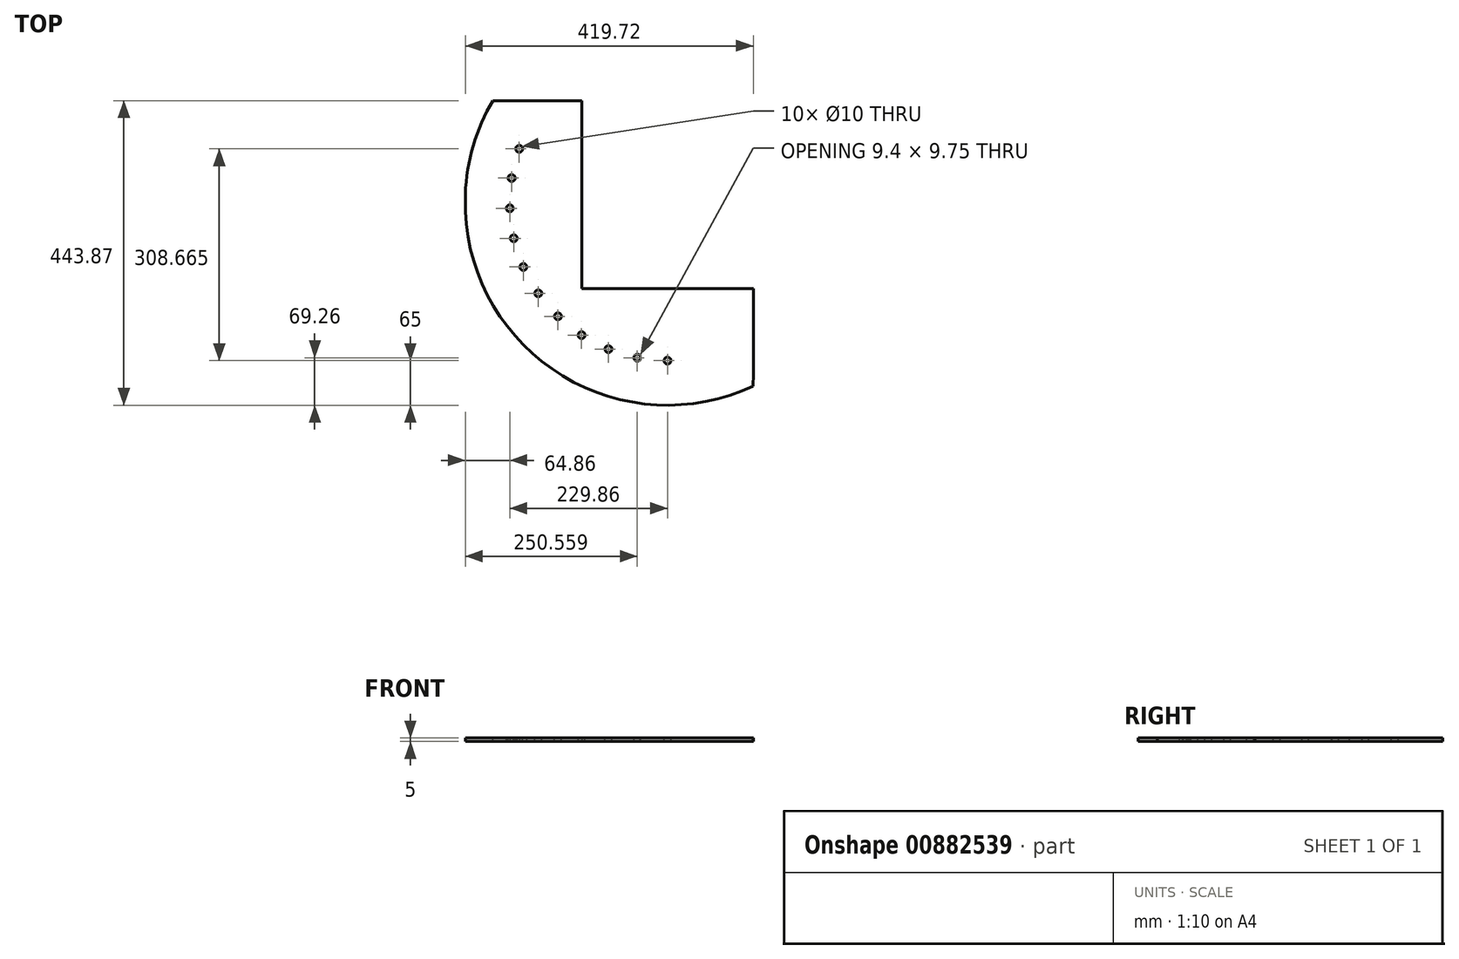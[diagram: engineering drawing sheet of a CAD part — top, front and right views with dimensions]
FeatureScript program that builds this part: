
annotation { "Feature Type Name" : "Feature", "Feature Type Description" : "" }
export const myFeature = defineFeature(function(context is Context, id is Id, definition is map)
    precondition{}
    {
        {
            var Q0;
            Q0=qCreatedBy(makeId("Top.planeOp"),FACE);
            var sketch = newSketch(context, id + "F0", { "sketchPlane" : qUnion([Q0])});
            skLineSegment(sketch, "E0.bottom", {"start": v(125, -125) * mm, "end": v(-125, -125) * mm});
            skLineSegment(sketch, "E0.top", {"start": v(125, 125) * mm, "end": v(-125, 125) * mm});
            skLineSegment(sketch, "E0.left", {"start": v(125, -125) * mm, "end": v(125, 125) * mm});
            skLineSegment(sketch, "E0.right", {"start": v(-125, -125) * mm, "end": v(-125, 125) * mm});
            skPoint(sketch, "E0.middle", {"position": v(0, 0) * mm});
            skLineSegment(sketch, "E1", {"start": v(0, 0) * mm, "end": v(-125, 0) * mm, "construction": true});
            skLineSegment(sketch, "E2.bottom", {"start": v(-349.96, 0) * mm, "end": v(0, 0) * mm});
            skLineSegment(sketch, "E2.left", {"start": v(-349.96, 0) * mm, "end": v(-349.96, 125) * mm});
            skLineSegment(sketch, "E2.right", {"start": v(125, 0) * mm, "end": v(125, 125) * mm});
            skLineSegment(sketch, "E3.MirrorCS", {"start": v(-349.96, 0) * mm, "end": v(-349.96, -249.62) * mm});
            skLineSegment(sketch, "E4.MirrorCS", {"start": v(-349.96, -249.62) * mm, "end": v(125, -249.62) * mm});
            skLineSegment(sketch, "E5.MirrorCS", {"start": v(125, 0) * mm, "end": v(125, -249.62) * mm});
            skLineSegment(sketch, "E6", {"start": v(-349.96, 125) * mm, "end": v(125, 125) * mm});
            skPoint(sketch, "E2.top.start.orphan", {"position": v(-349.96, 249.62) * mm});
            skPoint(sketch, "E7.orphan", {"position": v(125, 249.62) * mm});
            skLineSegment(sketch, "E8", {"start": v(-349.96, 29.15) * mm, "end": v(-125, 29.15) * mm});
            skLineSegment(sketch, "E9", {"start": v(-349.96, -249.62) * mm, "end": v(-349.96, -298.58) * mm});
            skLineSegment(sketch, "E10", {"start": v(-349.96, -298.58) * mm, "end": v(124.79, -298.58) * mm});
            skLineSegment(sketch, "E11", {"start": v(124.79, -298.58) * mm, "end": v(125, -249.62) * mm});
            skLineSegment(sketch, "E12", {"start": v(-294.72, 29.15) * mm, "end": v(-294.72, -298.58) * mm});
            skLineSegment(sketch, "E13", {"start": v(-294.72, 29.15) * mm, "end": v(-294.72, 125) * mm});
            skLineSegment(sketch, "E14", {"start": v(-294.72, 125) * mm, "end": v(-294.72, 148.87) * mm});
            skLineSegment(sketch, "E15", {"start": v(-294.72, 148.87) * mm, "end": v(-125.13, 148.87) * mm});
            skLineSegment(sketch, "E16", {"start": v(-125.13, 148.87) * mm, "end": v(-125, 125) * mm});
            skSolve(sketch);
        }
        {
            var Q0;
            {var subQ0=sQuery(id+"F0.wireOp",EDGE,"E8");var subQ1=sQuery(id+"F0.wireOp",EDGE,"E0.right");var subQ2=makeQuery(id+"F0.imprint","INTERSECT",VERTEX,{"derivedFrom":[subQ1,subQ0]});Q0=makeQuery(id+"F0.imprint","IMPRINT",FACE,{"disambiguationData":[TD([[makeQuery(id+"F0.imprint","IMPRINT",EDGE,{"disambiguationData":[TD([[subQ2,1.0]])],"derivedFrom":subQ1}),1.0]])]});}
            var Q1;
            {var subQ5=sQuery(id+"F0.wireOp",EDGE,"E0.bottom");Q1=makeQuery(id+"F0.imprint","IMPRINT",FACE,{"disambiguationData":[TD([[makeQuery(id+"F0.imprint","IMPRINT",EDGE,{"derivedFrom":subQ5}),1.0]])]});}
            var Q2;
            {var subQ0=sQuery(id+"F0.wireOp",EDGE,"E11");Q2=makeQuery(id+"F0.imprint","IMPRINT",FACE,{"disambiguationData":[TD([[makeQuery(id+"F0.imprint","IMPRINT",EDGE,{"derivedFrom":subQ0}),1.0]])]});}
            var Q3;
            {var subQ4=sQuery(id+"F0.wireOp",EDGE,"E6");var subQ5=sQuery(id+"F0.wireOp",EDGE,"E0.right");var subQ6=makeQuery(id+"F0.imprint","INTERSECT",VERTEX,{"derivedFrom":[subQ5,subQ4]});Q3=makeQuery(id+"F0.imprint","IMPRINT",FACE,{"disambiguationData":[TD([[makeQuery(id+"F0.imprint","IMPRINT",EDGE,{"disambiguationData":[TD([[subQ6,1.0]])],"derivedFrom":subQ5}),1.0]])]});}
            var Q4;
            {var subQ2=sQuery(id+"F0.wireOp",EDGE,"E14");Q4=makeQuery(id+"F0.imprint","IMPRINT",FACE,{"disambiguationData":[TD([[makeQuery(id+"F0.imprint","IMPRINT",EDGE,{"derivedFrom":subQ2}),-1.0]])]});}
            extrude(context, id + "F1", {"entities" : qUnion([Q0, Q1, Q2, Q3, Q4]), "depth" : 5 * mm, "offsetDistance" : 25 * mm});
        }
        {
            var Q0;
            Q0=makeQuery(id+"F1.opExtrude","CAP_FACE",FACE,{"disambiguationData":[OSD([sQuery(id+"F0.wireOp",EDGE,"E0.bottom"),sQuery(id+"F0.wireOp",EDGE,"E0.top"),sQuery(id+"F0.wireOp",EDGE,"E0.left"),sQuery(id+"F0.wireOp",EDGE,"E0.right"),sQuery(id+"F0.wireOp",EDGE,"E2.top"),sQuery(id+"F0.wireOp",EDGE,"E2.left"),sQuery(id+"F0.wireOp",EDGE,"E2.right"),sQuery(id+"F0.wireOp",EDGE,"E3.MirrorCS"),sQuery(id+"F0.wireOp",EDGE,"E4.MirrorCS"),sQuery(id+"F0.wireOp",EDGE,"E5.MirrorCS")])],"isStart":false});
            var sketch = newSketch(context, id + "F2", { "sketchPlane" : qUnion([Q0])});
            skCircle(sketch, "E17", {"center": v(0, 0) * mm, "radius": 270 * mm});
            skCircle(sketch, "E18", {"center": v(0, 0) * mm, "radius": 190 * mm});
            skLineSegment(sketch, "E19", {"start": v(0, 0) * mm, "end": v(-270, 0) * mm, "construction": true});
            skCircle(sketch, "E20", {"center": v(0, 0) * mm, "radius": 230 * mm, "construction": true});
            skCircle(sketch, "E21", {"center": v(-216.13, 78.66) * mm, "radius": 40 * mm});
            skCircle(sketch, "E22", {"center": v(0, -230) * mm, "radius": 40 * mm});
            skLineSegment(sketch, "E23", {"start": v(-216.13, 78.66) * mm, "end": v(0, 0) * mm, "construction": true});
            skLineSegment(sketch, "E24", {"start": v(0, 0) * mm, "end": v(0, -230) * mm, "construction": true});
            skCircle(sketch, "E25", {"center": v(-216.13, 78.66) * mm, "radius": 5 * mm});
            skCircle(sketch, "E26.1.0", {"center": v(-227.17, 35.98) * mm, "radius": 5 * mm});
            skCircle(sketch, "E26.2.0", {"center": v(-229.86, -8.03) * mm, "radius": 5 * mm});
            skCircle(sketch, "E26.3.0", {"center": v(-224.1, -51.74) * mm, "radius": 5 * mm});
            skCircle(sketch, "E26.4.0", {"center": v(-210.12, -93.55) * mm, "radius": 5 * mm});
            skCircle(sketch, "E26.5.0", {"center": v(-188.4, -131.92) * mm, "radius": 5 * mm});
            skCircle(sketch, "E26.6.0", {"center": v(-159.77, -165.45) * mm, "radius": 5 * mm});
            skCircle(sketch, "E26.7.0", {"center": v(-125.27, -192.9) * mm, "radius": 5 * mm});
            skCircle(sketch, "E26.8.0", {"center": v(-86.16, -213.25) * mm, "radius": 5 * mm});
            skCircle(sketch, "E26.9.0", {"center": v(-43.89, -225.77) * mm, "radius": 5 * mm});
            skCircle(sketch, "E26.10.0", {"center": v(0, -230) * mm, "radius": 5 * mm});
            skLineSegment(sketch, "E26.anchor1", {"start": v(0, 0) * mm, "end": v(-216.13, 78.66) * mm, "construction": true});
            skSolve(sketch);
        }
        {
            var Q0;
            Q0=makeQuery(id+"F2.imprint","IMPRINT",FACE,{"disambiguationData":[TD([[makeQuery(id+"F2.imprint","IMPRINT",EDGE,{"derivedFrom":sQuery(id+"F2.wireOp",EDGE,"E26.10.0")}),1.0]])]});
            var Q1;
            {var subQ0=sQuery(id+"F2.wireOp",EDGE,"E26.9.0");var subQ1=sQuery(id+"F2.wireOp",EDGE,"E22");var subQ2=makeQuery(id+"F2.imprint","INTERSECT",VERTEX,{"disambiguationData":[OD(0.0)],"derivedFrom":[subQ1,subQ0]});Q1=makeQuery(id+"F2.imprint","IMPRINT",FACE,{"disambiguationData":[TD([[makeQuery(id+"F2.imprint","IMPRINT",EDGE,{"disambiguationData":[TD([[subQ2,-1.0]])],"derivedFrom":subQ1}),-1.0]])]});}
            var Q2;
            Q2=makeQuery(id+"F2.imprint","IMPRINT",FACE,{"disambiguationData":[TD([[makeQuery(id+"F2.imprint","IMPRINT",EDGE,{"derivedFrom":sQuery(id+"F2.wireOp",EDGE,"E26.8.0")}),1.0]])]});
            var Q3;
            Q3=makeQuery(id+"F2.imprint","IMPRINT",FACE,{"disambiguationData":[TD([[makeQuery(id+"F2.imprint","IMPRINT",EDGE,{"derivedFrom":sQuery(id+"F2.wireOp",EDGE,"E26.7.0")}),1.0]])]});
            var Q4;
            Q4=makeQuery(id+"F2.imprint","IMPRINT",FACE,{"disambiguationData":[TD([[makeQuery(id+"F2.imprint","IMPRINT",EDGE,{"derivedFrom":sQuery(id+"F2.wireOp",EDGE,"E26.5.0")}),1.0]])]});
            var Q5;
            Q5=makeQuery(id+"F2.imprint","IMPRINT",FACE,{"disambiguationData":[TD([[makeQuery(id+"F2.imprint","IMPRINT",EDGE,{"derivedFrom":sQuery(id+"F2.wireOp",EDGE,"E26.6.0")}),1.0]])]});
            var Q6;
            Q6=makeQuery(id+"F2.imprint","IMPRINT",FACE,{"disambiguationData":[TD([[makeQuery(id+"F2.imprint","IMPRINT",EDGE,{"derivedFrom":sQuery(id+"F2.wireOp",EDGE,"E26.4.0")}),1.0]])]});
            var Q7;
            Q7=makeQuery(id+"F2.imprint","IMPRINT",FACE,{"disambiguationData":[TD([[makeQuery(id+"F2.imprint","IMPRINT",EDGE,{"derivedFrom":sQuery(id+"F2.wireOp",EDGE,"E26.3.0")}),1.0]])]});
            var Q8;
            Q8=makeQuery(id+"F2.imprint","IMPRINT",FACE,{"disambiguationData":[TD([[makeQuery(id+"F2.imprint","IMPRINT",EDGE,{"derivedFrom":sQuery(id+"F2.wireOp",EDGE,"E26.2.0")}),1.0]])]});
            var Q9;
            {var subQ0=sQuery(id+"F2.wireOp",EDGE,"E26.1.0");var subQ1=sQuery(id+"F2.wireOp",EDGE,"E21");var subQ2=makeQuery(id+"F2.imprint","INTERSECT",VERTEX,{"disambiguationData":[OD(0.0)],"derivedFrom":[subQ1,subQ0]});Q9=makeQuery(id+"F2.imprint","IMPRINT",FACE,{"disambiguationData":[TD([[makeQuery(id+"F2.imprint","IMPRINT",EDGE,{"disambiguationData":[TD([[subQ2,-1.0]])],"derivedFrom":subQ1}),-1.0]])]});}
            var Q10;
            Q10=makeQuery(id+"F2.imprint","IMPRINT",FACE,{"disambiguationData":[TD([[makeQuery(id+"F2.imprint","IMPRINT",EDGE,{"derivedFrom":sQuery(id+"F2.wireOp",EDGE,"E25")}),1.0]])]});
            var Q11;
            {var subQ0=sQuery(id+"F2.wireOp",EDGE,"E26.1.0");var subQ1=sQuery(id+"F2.wireOp",EDGE,"E21");var subQ2=makeQuery(id+"F2.imprint","INTERSECT",VERTEX,{"disambiguationData":[OD(0.0)],"derivedFrom":[subQ1,subQ0]});Q11=makeQuery(id+"F2.imprint","IMPRINT",FACE,{"disambiguationData":[TD([[makeQuery(id+"F2.imprint","IMPRINT",EDGE,{"disambiguationData":[TD([[subQ2,-1.0]])],"derivedFrom":subQ1}),1.0]])]});}
            extrude(context, id + "F3", {"entities" : qUnion([Q0, Q1, Q2, Q3, Q4, Q5, Q6, Q7, Q8, Q9, Q10, Q11]), "operationType" : NewBodyOperationType.REMOVE, "oppositeDirection" : true, "depth" : 6 * mm, "offsetDistance" : 25 * mm});
        }
        {
            var Q0;
            Q0=makeQuery(id+"F1.opExtrude","CAP_FACE",FACE,{"disambiguationData":[OSD([sQuery(id+"F0.wireOp",EDGE,"E0.bottom"),sQuery(id+"F0.wireOp",EDGE,"E0.right"),sQuery(id+"F0.wireOp",EDGE,"E5.MirrorCS"),sQuery(id+"F0.wireOp",EDGE,"E8"),sQuery(id+"F0.wireOp",EDGE,"E10"),sQuery(id+"F0.wireOp",EDGE,"E11"),sQuery(id+"F0.wireOp",EDGE,"E12")])],"isStart":false});
            var sketch = newSketch(context, id + "F4", { "sketchPlane" : qUnion([Q0])});
            skCircle(sketch, "E27", {"center": v(0, 0) * mm, "radius": 295 * mm});
            skLineSegment(sketch, "E28", {"start": v(178.33, -235) * mm, "end": v(178.33, -361.67) * mm});
            skLineSegment(sketch, "E29", {"start": v(178.33, -361.67) * mm, "end": v(-429.48, -361.67) * mm});
            skLineSegment(sketch, "E30", {"start": v(-429.48, -361.67) * mm, "end": v(-429.48, 76.22) * mm});
            skLineSegment(sketch, "E31", {"start": v(-429.48, 76.22) * mm, "end": v(-284.98, 76.22) * mm});
            skSolve(sketch);
        }
        {
            var Q0;
            {var subQ0=sQuery(id+"F4.wireOp",EDGE,"E27");var subQ1=makeQuery(id+"F1.opExtrude","CAP_EDGE",EDGE,{"disambiguationData":[OSD([sQuery(id+"F0.wireOp",EDGE,"E12")])],"isStart":false});var subQ2=makeQuery(id+"F4.imprint","INTERSECT",VERTEX,{"disambiguationData":[OD(0.0)],"derivedFrom":[subQ1,subQ0]});Q0=makeQuery(id+"F4.imprint","IMPRINT",FACE,{"disambiguationData":[TD([[makeQuery(id+"F4.imprint","IMPRINT",EDGE,{"disambiguationData":[TD([[subQ2,-1.0]])],"derivedFrom":subQ0}),1.0]])]});}
            var Q1;
            {var subQ0=sQuery(id+"F4.wireOp",EDGE,"E27");var subQ1=makeQuery(id+"F1.opExtrude","CAP_EDGE",EDGE,{"disambiguationData":[OSD([sQuery(id+"F0.wireOp",EDGE,"E8")])],"isStart":false});var subQ2=makeQuery(id+"F4.imprint","INTERSECT",VERTEX,{"derivedFrom":[subQ1,subQ0]});Q1=makeQuery(id+"F4.imprint","IMPRINT",FACE,{"disambiguationData":[TD([[makeQuery(id+"F4.imprint","IMPRINT",EDGE,{"disambiguationData":[TD([[subQ2,-1.0]])],"derivedFrom":subQ0}),-1.0]])]});}
            var Q2;
            {var subQ11=sQuery(id+"F4.wireOp",EDGE,"E28");Q2=makeQuery(id+"F4.imprint","IMPRINT",FACE,{"disambiguationData":[TD([[makeQuery(id+"F4.imprint","IMPRINT",EDGE,{"derivedFrom":subQ11}),-1.0]])]});}
            var Q3;
            {var subQ5=makeQuery(id+"F1.opExtrude","CAP_EDGE",EDGE,{"disambiguationData":[OSD([sQuery(id+"F0.wireOp",EDGE,"E10")])],"isStart":false});Q3=makeQuery(id+"F4.imprint","IMPRINT",FACE,{"disambiguationData":[TD([[makeQuery(id+"F4.imprint","IMPRINT",EDGE,{"derivedFrom":subQ5}),1.0]])]});}
            var Q4;
            {var subQ0=sQuery(id+"F4.wireOp",EDGE,"E31");var subQ1=sQuery(id+"F4.wireOp",EDGE,"E27");var subQ2=makeQuery(id+"F4.imprint","INTERSECT",VERTEX,{"derivedFrom":[subQ1,subQ0]});Q4=makeQuery(id+"F4.imprint","IMPRINT",FACE,{"disambiguationData":[TD([[makeQuery(id+"F4.imprint","IMPRINT",EDGE,{"disambiguationData":[TD([[subQ2,-1.0]])],"derivedFrom":subQ1}),-1.0]])]});}
            var Q5;
            {var subQ0=sQuery(id+"F4.wireOp",EDGE,"E31");var subQ1=sQuery(id+"F4.wireOp",EDGE,"E27");var subQ2=makeQuery(id+"F4.imprint","INTERSECT",VERTEX,{"derivedFrom":[subQ1,subQ0]});Q5=makeQuery(id+"F4.imprint","IMPRINT",FACE,{"disambiguationData":[TD([[makeQuery(id+"F4.imprint","IMPRINT",EDGE,{"disambiguationData":[TD([[subQ2,1.0]])],"derivedFrom":subQ1}),-1.0]])]});}
            extrude(context, id + "F5", {"entities" : qUnion([Q0, Q1, Q2, Q3, Q4, Q5]), "operationType" : NewBodyOperationType.REMOVE, "oppositeDirection" : true, "depth" : 25 * mm, "offsetDistance" : 25 * mm});
        }
    });
